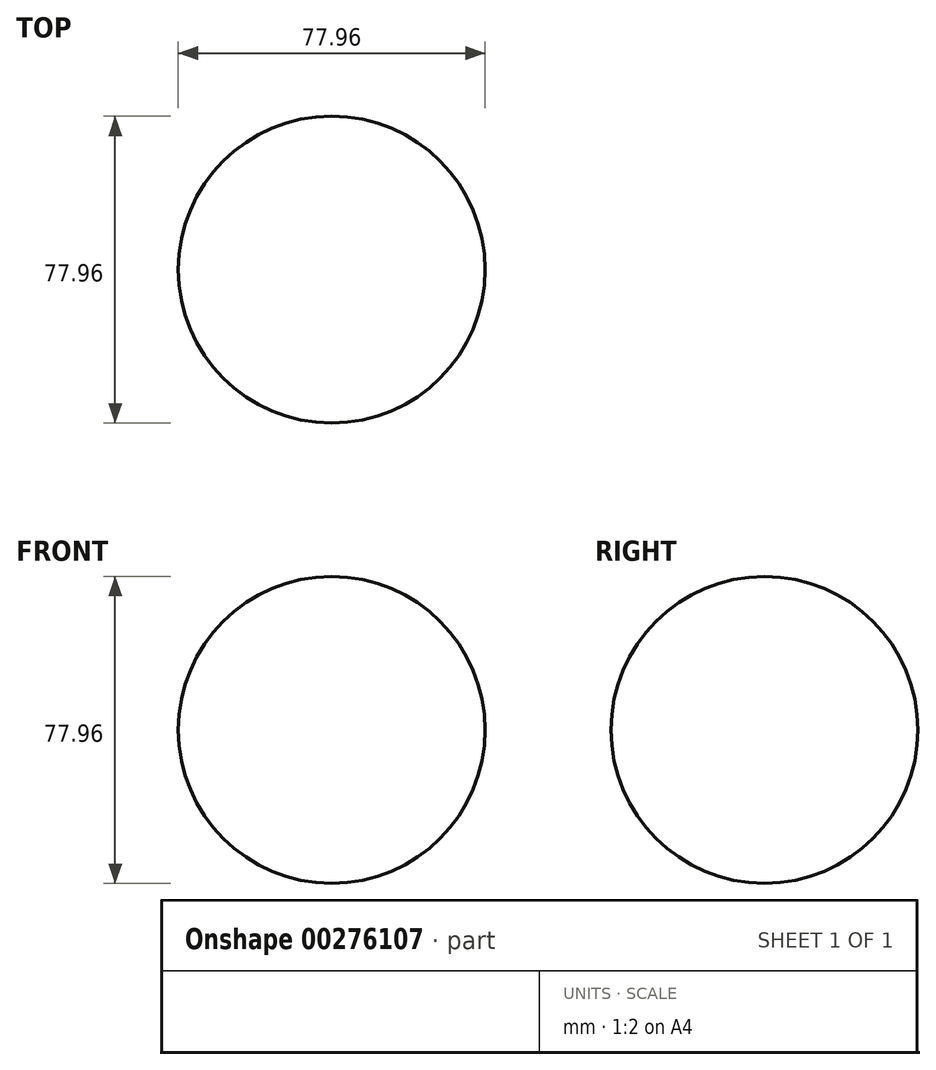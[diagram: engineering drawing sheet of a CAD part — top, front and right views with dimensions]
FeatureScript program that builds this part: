
annotation { "Feature Type Name" : "Feature", "Feature Type Description" : "" }
export const myFeature = defineFeature(function(context is Context, id is Id, definition is map)
    precondition{}
    {
        {
            var Q0;
            Q0=qCreatedBy(makeId("Front.planeOp"),FACE);
            var sketch = newSketch(context, id + "F0", { "sketchPlane" : qUnion([Q0])});
            skArc(sketch, "E0", {"start": v(0, 38.98) * mm, "mid": v(-38.98, 0) * mm, "end": v(0, -38.98) * mm});
            skLineSegment(sketch, "E1", {"start": v(0, 38.98) * mm, "end": v(0, -38.98) * mm});
            skSolve(sketch);
        }
        {
            var Q0;
            Q0=makeQuery(id+"F0.imprint","IMPRINT",FACE,{"disambiguationData":[TD([[makeQuery(id+"F0.imprint","IMPRINT",EDGE,{"derivedFrom":sQuery(id+"F0.wireOp",EDGE,"E0")}),1.0]])]});
            var Q1;
            Q1=sQuery(id+"F0.wireOp",EDGE,"E1");
            revolve(context, id + "F1", {"entities" : qUnion([Q0]), "axis" : qUnion([Q1]), "revolveType" : RevolveType.FULL});
        }
    });
